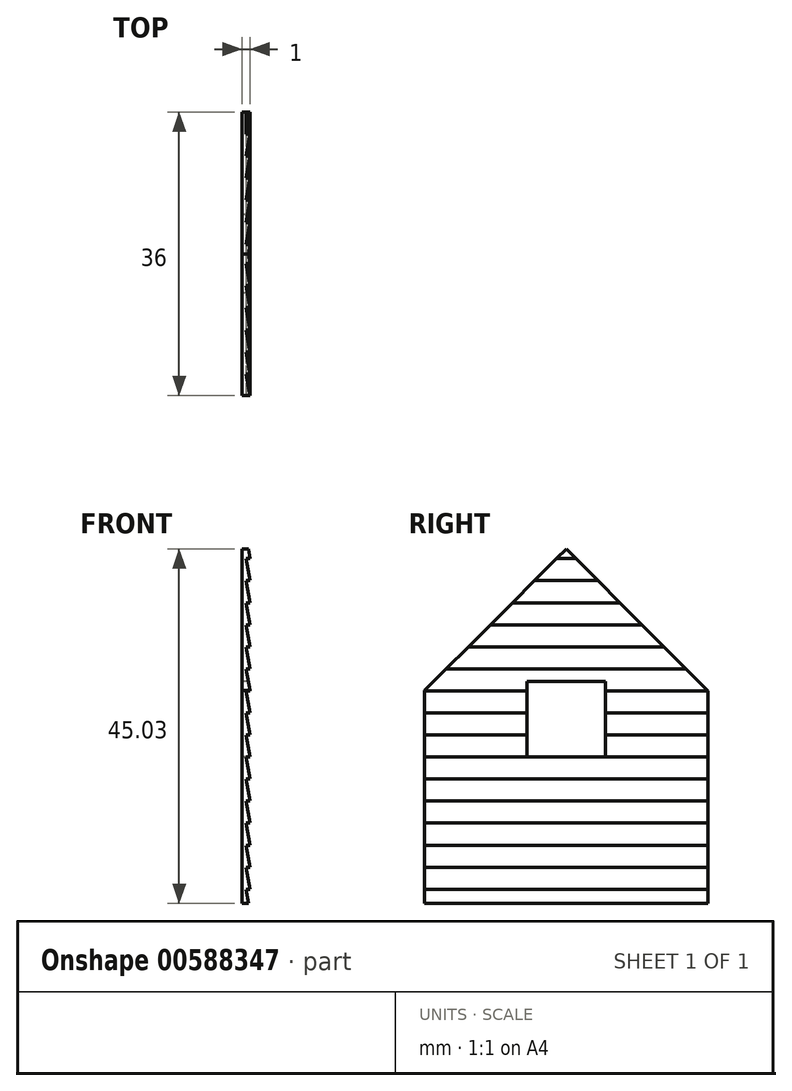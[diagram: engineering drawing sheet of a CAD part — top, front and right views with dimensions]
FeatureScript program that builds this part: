
annotation { "Feature Type Name" : "Feature", "Feature Type Description" : "" }
export const myFeature = defineFeature(function(context is Context, id is Id, definition is map)
    precondition{}
    {
        {
            var Q0;
            Q0=qCreatedBy(makeId("Right.planeOp"),FACE);
            var sketch = newSketch(context, id + "F0", { "sketchPlane" : qUnion([Q0])});
            skLineSegment(sketch, "E0", {"start": v(-53.46, 53.94) * mm, "end": v(-71.46, 35.94) * mm});
            skLineSegment(sketch, "E1", {"start": v(-53.46, 53.94) * mm, "end": v(-35.46, 35.94) * mm});
            skLineSegment(sketch, "E2", {"start": v(-70.46, 8.94) * mm, "end": v(-36.46, 8.94) * mm});
            skLineSegment(sketch, "E3", {"start": v(-71.46, 8.94) * mm, "end": v(-70.46, 8.94) * mm});
            skLineSegment(sketch, "E4", {"start": v(-35.46, 8.94) * mm, "end": v(-36.46, 8.94) * mm});
            skLineSegment(sketch, "E5", {"start": v(-71.46, 35.94) * mm, "end": v(-71.46, 8.94) * mm});
            skLineSegment(sketch, "E6", {"start": v(-35.46, 35.94) * mm, "end": v(-35.46, 33.14) * mm});
            skLineSegment(sketch, "E7", {"start": v(-35.46, 33.14) * mm, "end": v(-35.46, 30.34) * mm});
            skLineSegment(sketch, "E8", {"start": v(-35.46, 30.34) * mm, "end": v(-35.46, 27.54) * mm});
            skLineSegment(sketch, "E9", {"start": v(-35.46, 27.54) * mm, "end": v(-35.46, 24.74) * mm});
            skLineSegment(sketch, "E10", {"start": v(-35.46, 24.74) * mm, "end": v(-35.46, 21.94) * mm});
            skLineSegment(sketch, "E11", {"start": v(-35.46, 21.94) * mm, "end": v(-35.46, 19.14) * mm});
            skLineSegment(sketch, "E12", {"start": v(-35.46, 19.14) * mm, "end": v(-35.46, 16.34) * mm});
            skLineSegment(sketch, "E13", {"start": v(-35.46, 16.34) * mm, "end": v(-35.46, 13.54) * mm});
            skLineSegment(sketch, "E14", {"start": v(-35.46, 13.54) * mm, "end": v(-35.46, 10.74) * mm});
            skLineSegment(sketch, "E15", {"start": v(-35.46, 10.74) * mm, "end": v(-35.46, 8.94) * mm});
            skLineSegment(sketch, "E16", {"start": v(-35.46, 35.94) * mm, "end": v(-48.46, 35.94) * mm});
            skLineSegment(sketch, "E17", {"start": v(-35.46, 33.14) * mm, "end": v(-48.46, 33.14) * mm});
            skLineSegment(sketch, "E18", {"start": v(-35.46, 30.34) * mm, "end": v(-48.46, 30.34) * mm});
            skLineSegment(sketch, "E19", {"start": v(-35.46, 27.54) * mm, "end": v(-71.46, 27.54) * mm});
            skLineSegment(sketch, "E20", {"start": v(-35.46, 24.74) * mm, "end": v(-71.46, 24.74) * mm});
            skLineSegment(sketch, "E21", {"start": v(-35.46, 21.94) * mm, "end": v(-71.46, 21.94) * mm});
            skLineSegment(sketch, "E22", {"start": v(-35.46, 19.14) * mm, "end": v(-71.46, 19.14) * mm});
            skLineSegment(sketch, "E23", {"start": v(-35.46, 16.34) * mm, "end": v(-71.46, 16.34) * mm});
            skLineSegment(sketch, "E24", {"start": v(-35.46, 13.54) * mm, "end": v(-71.46, 13.54) * mm});
            skLineSegment(sketch, "E25", {"start": v(-35.46, 10.74) * mm, "end": v(-71.46, 10.74) * mm});
            skLineSegment(sketch, "E26.trimOffspring", {"start": v(-58.46, 33.14) * mm, "end": v(-71.46, 33.14) * mm});
            skLineSegment(sketch, "E27.trimOffspring", {"start": v(-58.46, 30.34) * mm, "end": v(-71.46, 30.34) * mm});
            skLineSegment(sketch, "E28", {"start": v(-57.46, 36.94) * mm, "end": v(-48.46, 36.94) * mm});
            skLineSegment(sketch, "E29", {"start": v(-57.46, 36.94) * mm, "end": v(-58.46, 36.94) * mm});
            skLineSegment(sketch, "E30", {"start": v(-58.46, 36.94) * mm, "end": v(-58.46, 26.94) * mm});
            skLineSegment(sketch, "E31", {"start": v(-48.46, 36.94) * mm, "end": v(-48.46, 26.94) * mm});
            skLineSegment(sketch, "E32", {"start": v(-48.46, 26.94) * mm, "end": v(-58.46, 26.94) * mm});
            skLineSegment(sketch, "E33.trimOffspring", {"start": v(-58.46, 35.94) * mm, "end": v(-71.46, 35.94) * mm});
            skSolve(sketch);
        }
        {
            var Q0;
            Q0=makeQuery(id+"F0.imprint","IMPRINT",FACE,{"disambiguationData":[TD([[makeQuery(id+"F0.imprint","IMPRINT",EDGE,{"derivedFrom":sQuery(id+"F0.wireOp",EDGE,"E2")}),1.0]])]});
            extrude(context, id + "F1", {"entities" : qUnion([Q0]), "depth" : .5 * mm, "offsetDistance" : 25 * mm});
        }
        {
            var Q0;
            Q0=makeQuery(id+"F1.opExtrude","SWEPT_FACE",FACE,{"disambiguationData":[OSD([sQuery(id+"F0.wireOp",EDGE,"E5")])]});
            var sketch = newSketch(context, id + "F2", { "sketchPlane" : qUnion([Q0])});
            skPoint(sketch, "E34.endSnap0", {"position": v(0.5, 9.84) * mm});
            skLineSegment(sketch, "E35", {"start": v(0.82, 8.94) * mm, "end": v(0.5, 10.74) * mm});
            skLineSegment(sketch, "E36", {"start": v(0, 8.94) * mm, "end": v(0.82, 8.94) * mm});
            skPoint(sketch, "E37.start.orphan", {"position": v(0.5, 7.94) * mm});
            skLineSegment(sketch, "E38", {"start": v(0.5, 10.74) * mm, "end": v(1, 10.74) * mm});
            skLineSegment(sketch, "E39", {"start": v(1, 13.54) * mm, "end": v(0.5, 13.54) * mm});
            skLineSegment(sketch, "E40", {"start": v(0.5, 13.54) * mm, "end": v(1, 10.74) * mm});
            skLineSegment(sketch, "E41", {"start": v(0.5, 16.34) * mm, "end": v(1, 13.54) * mm});
            skLineSegment(sketch, "E42", {"start": v(0.5, 16.34) * mm, "end": v(1, 16.34) * mm});
            skLineSegment(sketch, "E43", {"start": v(1, 16.34) * mm, "end": v(0.5, 19.14) * mm});
            skLineSegment(sketch, "E44", {"start": v(0.5, 19.14) * mm, "end": v(1, 19.14) * mm});
            skLineSegment(sketch, "E45", {"start": v(1, 19.14) * mm, "end": v(0.5, 21.94) * mm});
            skLineSegment(sketch, "E46", {"start": v(0, 8.94) * mm, "end": v(0, 56.3) * mm});
            skLineSegment(sketch, "E47", {"start": v(0.5, 54.66) * mm, "end": v(0, 54.66) * mm});
            skLineSegment(sketch, "E48", {"start": v(0.5, 52.74) * mm, "end": v(1, 52.74) * mm});
            skLineSegment(sketch, "E49", {"start": v(1, 52.74) * mm, "end": v(0.66, 54.66) * mm});
            skLineSegment(sketch, "E50", {"start": v(0.5, 54.66) * mm, "end": v(0.66, 54.66) * mm});
            skLineSegment(sketch, "E51", {"start": v(0.5, 49.94) * mm, "end": v(1, 49.94) * mm});
            skLineSegment(sketch, "E52", {"start": v(1, 49.94) * mm, "end": v(0.5, 52.74) * mm});
            skLineSegment(sketch, "E53", {"start": v(0.5, 47.14) * mm, "end": v(1, 47.14) * mm});
            skLineSegment(sketch, "E54", {"start": v(1, 47.14) * mm, "end": v(0.5, 49.94) * mm});
            skLineSegment(sketch, "E55", {"start": v(0.5, 44.34) * mm, "end": v(1, 44.34) * mm});
            skLineSegment(sketch, "E56", {"start": v(1, 44.34) * mm, "end": v(0.5, 47.14) * mm});
            skLineSegment(sketch, "E57", {"start": v(0.5, 41.54) * mm, "end": v(1, 41.54) * mm});
            skLineSegment(sketch, "E58", {"start": v(1, 41.54) * mm, "end": v(0.5, 44.34) * mm});
            skLineSegment(sketch, "E59", {"start": v(0.5, 38.74) * mm, "end": v(1, 38.74) * mm});
            skLineSegment(sketch, "E60", {"start": v(1, 38.74) * mm, "end": v(0.5, 41.54) * mm});
            skLineSegment(sketch, "E61", {"start": v(0.5, 35.94) * mm, "end": v(1, 35.94) * mm});
            skLineSegment(sketch, "E62", {"start": v(1, 35.94) * mm, "end": v(0.5, 38.74) * mm});
            skLineSegment(sketch, "E63", {"start": v(0.5, 33.14) * mm, "end": v(1, 33.14) * mm});
            skLineSegment(sketch, "E64", {"start": v(1, 33.14) * mm, "end": v(0.5, 35.94) * mm});
            skLineSegment(sketch, "E65", {"start": v(0.5, 30.34) * mm, "end": v(1, 30.34) * mm});
            skLineSegment(sketch, "E66", {"start": v(1, 30.34) * mm, "end": v(0.5, 33.14) * mm});
            skLineSegment(sketch, "E67", {"start": v(0.5, 27.54) * mm, "end": v(1, 27.54) * mm});
            skLineSegment(sketch, "E68", {"start": v(1, 27.54) * mm, "end": v(0.5, 30.34) * mm});
            skLineSegment(sketch, "E69", {"start": v(0.5, 24.74) * mm, "end": v(1, 24.74) * mm});
            skLineSegment(sketch, "E70", {"start": v(1, 24.74) * mm, "end": v(0.5, 27.54) * mm});
            skLineSegment(sketch, "E71", {"start": v(0.5, 21.94) * mm, "end": v(1, 21.94) * mm});
            skLineSegment(sketch, "E72", {"start": v(1, 21.94) * mm, "end": v(0.5, 24.74) * mm});
            skSolve(sketch);
        }
        {
            var Q0;
            {var subQ0=sQuery(id+"F2.wireOp",EDGE,"E35");Q0=makeQuery(id+"F2.imprint","IMPRINT",FACE,{"disambiguationData":[TD([[makeQuery(id+"F2.imprint","IMPRINT",EDGE,{"derivedFrom":subQ0}),1.0]])]});}
            extrude(context, id + "F3", {"entities" : qUnion([Q0]), "operationType" : NewBodyOperationType.ADD, "oppositeDirection" : true, "depth" : 36 * mm, "offsetDistance" : 25 * mm});
        }
        {
            var Q0;
            Q0=makeQuery(id+"F2.imprint","IMPRINT",FACE,{"disambiguationData":[TD([[makeQuery(id+"F2.imprint","IMPRINT",EDGE,{"derivedFrom":sQuery(id+"F2.wireOp",EDGE,"E38")}),1.0]])]});
            extrude(context, id + "F4", {"entities" : qUnion([Q0]), "operationType" : NewBodyOperationType.ADD, "oppositeDirection" : true, "depth" : 36 * mm, "offsetDistance" : 25 * mm});
        }
        {
            var Q0;
            {var subQ4=sQuery(id+"F0.wireOp",EDGE,"E28");Q0=makeQuery(id+"F0.imprint","IMPRINT",FACE,{"disambiguationData":[TD([[makeQuery(id+"F0.imprint","IMPRINT",EDGE,{"derivedFrom":subQ4}),-1.0]])]});}
            extrude(context, id + "F5", {"entities" : qUnion([Q0]), "operationType" : NewBodyOperationType.REMOVE, "depth" : 25 * mm, "offsetDistance" : 25 * mm});
        }
        {
            var Q0;
            Q0=makeQuery(id+"F4.boolean.opBoolean","MERGE",FACE,{"derivedFrom":[makeQuery(id+"F1.opExtrude","CAP_FACE",FACE,{"disambiguationData":[OSD([sQuery(id+"F0.wireOp",EDGE,"E2"),sQuery(id+"F0.wireOp",EDGE,"E3"),sQuery(id+"F0.wireOp",EDGE,"E4"),sQuery(id+"F0.wireOp",EDGE,"E5"),sQuery(id+"F0.wireOp",EDGE,"E15"),sQuery(id+"F0.wireOp",EDGE,"E25")])],"isStart":true}),makeQuery(id+"F4.opExtrude","SWEPT_FACE",FACE,{"disambiguationData":[OSD([sQuery(id+"F2.wireOp",EDGE,"E46")])]})]});
            var sketch = newSketch(context, id + "F6", { "sketchPlane" : qUnion([Q0])});
            skLineSegment(sketch, "E73", {"start": v(35.46, 35.92) * mm, "end": v(53.48, 53.97) * mm});
            skLineSegment(sketch, "E74", {"start": v(53.48, 53.97) * mm, "end": v(71.46, 36) * mm});
            skLineSegment(sketch, "E75", {"start": v(71.46, 36) * mm, "end": v(35.46, 35.92) * mm});
            skLineSegment(sketch, "E76", {"start": v(35.46, 54.66) * mm, "end": v(71.46, 54.66) * mm});
            skLineSegment(sketch, "E77", {"start": v(71.46, 54.66) * mm, "end": v(71.46, 36) * mm});
            skLineSegment(sketch, "E78", {"start": v(35.46, 54.66) * mm, "end": v(35.46, 35.92) * mm});
            skSolve(sketch);
        }
        {
            var Q0;
            Q0=makeQuery(id+"F6.imprint","IMPRINT",FACE,{"disambiguationData":[TD([[makeQuery(id+"F6.imprint","IMPRINT",EDGE,{"derivedFrom":sQuery(id+"F6.wireOp",EDGE,"E73")}),1.0]])]});
            extrude(context, id + "F7", {"entities" : qUnion([Q0]), "operationType" : NewBodyOperationType.REMOVE, "oppositeDirection" : true, "depth" : 25 * mm, "offsetDistance" : 25 * mm});
        }
        {
            var Q0;
            Q0=makeQuery(id+"F5.boolean.opBoolean","COPY",FACE,{"derivedFrom":makeQuery(id+"F5.opExtrude","SWEPT_FACE",FACE,{"disambiguationData":[OSD([sQuery(id+"F0.wireOp",EDGE,"E28"),sQuery(id+"F0.wireOp",EDGE,"E29")])]})});
            extrude(context, id + "F8", {"entities" : qUnion([Q0]), "operationType" : NewBodyOperationType.REMOVE, "oppositeDirection" : true, "depth" : 0.22 * mm, "offsetDistance" : 25 * mm});
        }
    });
